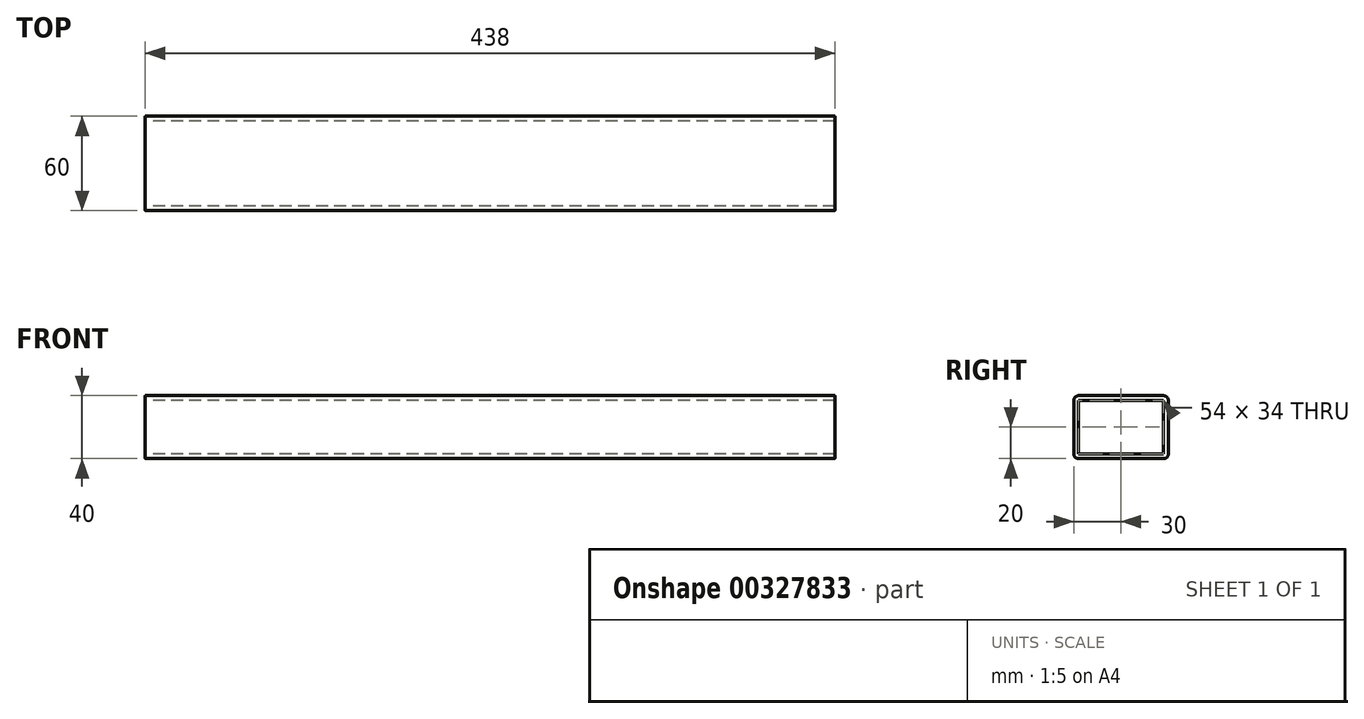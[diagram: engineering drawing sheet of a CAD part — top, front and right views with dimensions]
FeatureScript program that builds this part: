
annotation { "Feature Type Name" : "Feature", "Feature Type Description" : "" }
export const myFeature = defineFeature(function(context is Context, id is Id, definition is map)
    precondition{}
    {
        {
            var Q0;
            Q0=qCreatedBy(makeId("Right.planeOp"),FACE);
            var sketch = newSketch(context, id + "F0", { "sketchPlane" : qUnion([Q0])});
            skLineSegment(sketch, "E0.bottom", {"start": v(0, 0) * mm, "end": v(-54, 0) * mm});
            skLineSegment(sketch, "E0.top", {"start": v(0, 34) * mm, "end": v(-54, 34) * mm});
            skLineSegment(sketch, "E0.left", {"start": v(0, 0) * mm, "end": v(0, 34) * mm});
            skLineSegment(sketch, "E0.right", {"start": v(-54, 0) * mm, "end": v(-54, 34) * mm});
            skLineSegment(sketch, "E1.0", {"start": v(0, 37) * mm, "end": v(-54, 37) * mm});
            skLineSegment(sketch, "E2.0", {"start": v(3, 0) * mm, "end": v(3, 34) * mm});
            skLineSegment(sketch, "E3.0", {"start": v(0, -3) * mm, "end": v(-54, -3) * mm});
            skLineSegment(sketch, "E4.0", {"start": v(-57, 0) * mm, "end": v(-57, 34) * mm});
            skArc(sketch, "E5.filletArc", {"start": v(-54, 37) * mm, "mid": v(-56.12, 36.12) * mm, "end": v(-57, 34) * mm});
            skArc(sketch, "E6.filletArc", {"start": v(3, 34) * mm, "mid": v(2.12, 36.12) * mm, "end": v(0, 37) * mm});
            skArc(sketch, "E7.filletArc", {"start": v(0, -3) * mm, "mid": v(2.12, -2.12) * mm, "end": v(3, 0) * mm});
            skArc(sketch, "E8.filletArc", {"start": v(-57, 0) * mm, "mid": v(-56.12, -2.12) * mm, "end": v(-54, -3) * mm});
            skSolve(sketch);
        }
        {
            var Q0;
            Q0 = qSketchRegion(id + "F0", true);
            extrude(context, id + "F1", {"entities" : qUnion([Q0]), "endBound" : BoundingType.SYMMETRIC, "depth" : 438 * mm, "offsetDistance" : 25 * mm});
        }
    });
